# Revit family: шаблон семейства 2017
name_source: partatom
category: Датчики
revit_build: Autodesk Revit 2017 (Build: 20170118_1100(x64)
units: mm (PartAtom-declared; Revit-internal decimal feet)

## family parameters
Всегда вертикально = Нет
На основе рабочей плоскости = Нет
Общий = Нет
При загрузке вырезать с полостями = Нет
Размер круглого соединителя = Использовать диаметр
Сохранять ориентацию аннотаций = Нет
Тип детали = Нормальный
Точка расчета площади = Нет

## types (1)
- STS-123 Извещатель охранный (передачик)
    ADSK_URL страницы изделия = https://stilsoft.ru
    ADSK_Единица измерения = шт.
    ADSK_Завод-изготовитель = ООО «Основа Безопасности»
    ADSK_Количество = 1
    ADSK_Марка = СТВФ.425151.002
    ADSK_Масса = 1
    ADSK_Наименование = Извещатель охранный STS-123
    d_короба = 20 мм
    Взаимозаменяемость однотипных блоков = да
    Время восстановления дежурного режима, не более, с = 10
    Время технической готовности извещателя, не более, с = 30
    Выдача тревожного извещения при вскрытии корпуса = да
    Диапазон рабочих температур, °С = от –40 до +70
    Длина волны, нм = 920
    Длина зоны обнаружения, м = от 1 до 100
    Длительность тревожного извещения, не менее, с = 2 или 5 (настр.)
    Защита от попадания внутрь твердых тел (пыли) и воды = IP 54
    Индикация «уровень» отображает три режима состояния в зависимости от уровня принимаемого сигнала = да
    Информативность по шине RS-485 = 8
    Информативность по шлейфу = 5
    Коэффициент запаса по оптическому сигналу (на максимальной дальности) = 100
    Максимальные оптические потери (на максимальной дальности), не более, % = 99
    Наличие в приемнике светодиодных индикаторов «тревога» и «питание» = да
    Наличие семисегментного цифрового индикатора уровня сигнала = да
    Напряжение электропитания постоянного тока, В = от 9 до 30
    Наработка на ложное срабатывание, не менее, ч = 1200
    Обеспечен интеллектуальный режим обработки сигнала, позволяющий отличать прямые и переотраженные ИК-лучи, попадающие на оптическое окно приемника, и формирующий извещение «ТРЕВОГА» при пересечении прямого ИК-луча при мешающем воздействии переотраженных ИК-лучей = да
    Обеспечение дискретного изменения чувствительности четырех ступеней в диапазоне, мс = от 50 до 700
    Поворот оптического узла по вертикали, не менее = 20°
    Поворот оптического узла по горизонтали, не менее = 180°
    Помехозащищенность изделия в диапазоне, мс = от 35 до 280
    Помехоустойчивость изделия от солнца и источников освещения, питающихся от источников постоянного тока, не менее, лк = 30000
    Помехоустойчивость изделия от электроосветительных приборов, питающихся от сети переменного тока, не менее, лк = 2000
    Потребляемый ток обогрева каждого блока при напряжении электропитания 12 В, не более, А = 0.15
    Потребляемый ток при напряжении электропитания 12 В передатчик не более, мА = 10
    Режим работы = круглосуточно
    Сохранение работоспособности в условиях воздействия повышенной относительной влажности при температуре 30°С, % = 98
    Средняя наработка на отказ изделия в дежурном режиме, часов = 60000
    Тип интерфейса = RS-485, TTL
    Формирование сигнала «ТРЕВОГА» путем размыкания контактов выходной цепи = да
    Число ИК-лучей, работающих синхронно, шт = 2
    Число рабочих каналов ИК-излучения, шт. = 4
    Эффективная ширина излучения, см = 20
